# Revit family: GR_Адаптер линейный_Муфта(n)_TL-КСД-У_П_R21
name_source: partatom
category: Соединительные детали воздуховодов
units: mm (PartAtom-declared; Revit-internal decimal feet)

## family parameters
Всегда вертикально = Да
Заголовок OmniClass = Metal Ducts
На основе рабочей плоскости = Нет
Номер OmniClass = 23.75.70.14.31
Общий = Нет
При загрузке вырезать с полостями = Нет
Размер круглого соединителя = Использовать диаметр
Тип детали = Мультипорт

## types (10) — shared parameters
ADSK_URL страницы изделия = https://grilles.ru
ADSK_Версия Revit = 2021
ADSK_Единица измерения = шт.
ADSK_Завод-изготовитель = ООО "ВЕНТРЕШЕТКИКОМ"
ADSK_Количество = 1
ADSK_Материал = ADSK_Оцинкованная сталь
ADSK_Наименование = TL-КСД-У-П, адаптер вентиляционной решётки радиальный
Изготовитель = ООО "ВЕНТРЕШЕТКИКОМ"
Корпус_Металл_Толщина = 1 мм
Муфта_Металл_Толщина = 1 мм
zero-valued in all types: Отметка по умолчанию

## per-type parameters (varying)
| type | ADSK_Код изделия | W | Высота диффузора | Корпус_Высота | Корпус_Длина | Решетка_отступ | Решётка_Высота | Щёчки_Высота |
| TLS-КСД-У-П 20 | 000200 | 113 мм | 65 мм | 75 мм | 300 мм | 59 мм | 116 мм | 13 мм |
| TLS-КСД-У-П 30 | 000200 | 113 мм | 65 мм | 75 мм | 310 мм | 64 мм | 126 мм | 13 мм |
| TLS-КСД-У-П 40 | 000200 | 143 мм | 65 мм | 105 мм | 320 мм | 69 мм | 136 мм | 13 мм |
| TLS-КСД-У-П 50 | 000200 | 143 мм | 65 мм | 105 мм | 330 мм | 74 мм | 146 мм | 13 мм |
| TLS-КСД-У-П 60 | 000200 | 178 мм | 65 мм | 140 мм | 340 мм | 79 мм | 156 мм | 13 мм |
| TLS-КСД-У-П 70 | 000200 | 178 мм | 65 мм | 140 мм | 350 мм | 84 мм | 166 мм | 13 мм |
| TLM-КСД-У-П 40 | 000201 | 156 мм | 76 мм | 105 мм | 300 мм | 69 мм | 136 мм | 24 мм |
| TLM-КСД-У-П 50 | 000201 | 156 мм | 76 мм | 105 мм | 310 мм | 74 мм | 146 мм | 24 мм |
| TLL-КСД-У-П 60 | 000202 | 202 мм | 102 мм | 140 мм | 400 мм | 99 мм | 196 мм | 26 мм |
| TLL-КСД-У-П 70 | 000202 | 202 мм | 102 мм | 140 мм | 410 мм | 104 мм | 206 мм | 26 мм |

note: column(s) folded — value = type name in every type: ADSK_Марка
